# Revit family: RT450
name_source: partatom
category: Generic Models
units: mm (PartAtom-declared; Revit-internal decimal feet)

## family parameters
Always vertical = No
Can host rebar = No
Cut with Voids When Loaded = No
Part Type = Normal
Room Calculation Point = No
Round Connector Dimension = Use Diameter
Shared = No
Work Plane-Based = Yes

## types (1)
- NBS Standard Parameters
    BIMObjectName = Metpro_Metprolibrary_Cabletray_General
    Color = Grey
    Default Elevation = 1219 mm
    Description = RT450 = 450mm Rollatray
    DurationUnit = 1 Year
    Finish = Pre-Galvanised, dry oil to touch
    Manufacturer = Metpro Ltd
    ManufacturerName = Metpro ltd
    ManufacturerURL = www.metpro.co.uk
    Material = Steel
    ModelNumber = RT450
    ModelReference = Cable Tray
    NBSDescription = Cable Tray
    NBSReference = 90-55-10/335
    Name = RT450 - Rollatray
    NominalHeight = 4 mm  [stored 0.0131234 ft]
    NominalLength = 15000 mm  [stored 49.2126 ft]
    NominalWidth = 450 mm  [stored 1.47638 ft]
    ProductInformation = www.metpro.co.uk/pdf/RT450.pdf
    Shape = Flat
    Size = 450mm
    URL = www.metpro.co.uk
    Uniclass2 = Pr_65_70_11_17
    Version = 1
    WarrantyDurationUnit = 12 Months
    WarrantyGuarantorParts = 12 Months
    Weight = 34.8kg

note: [stored X ft] marks values corroborated as IEEE doubles in the binary element streams (Revit-internal decimal feet)

## geometry (parser evidence)
native form markers: Sweep x2
no freeform markers — native parametric forms only
